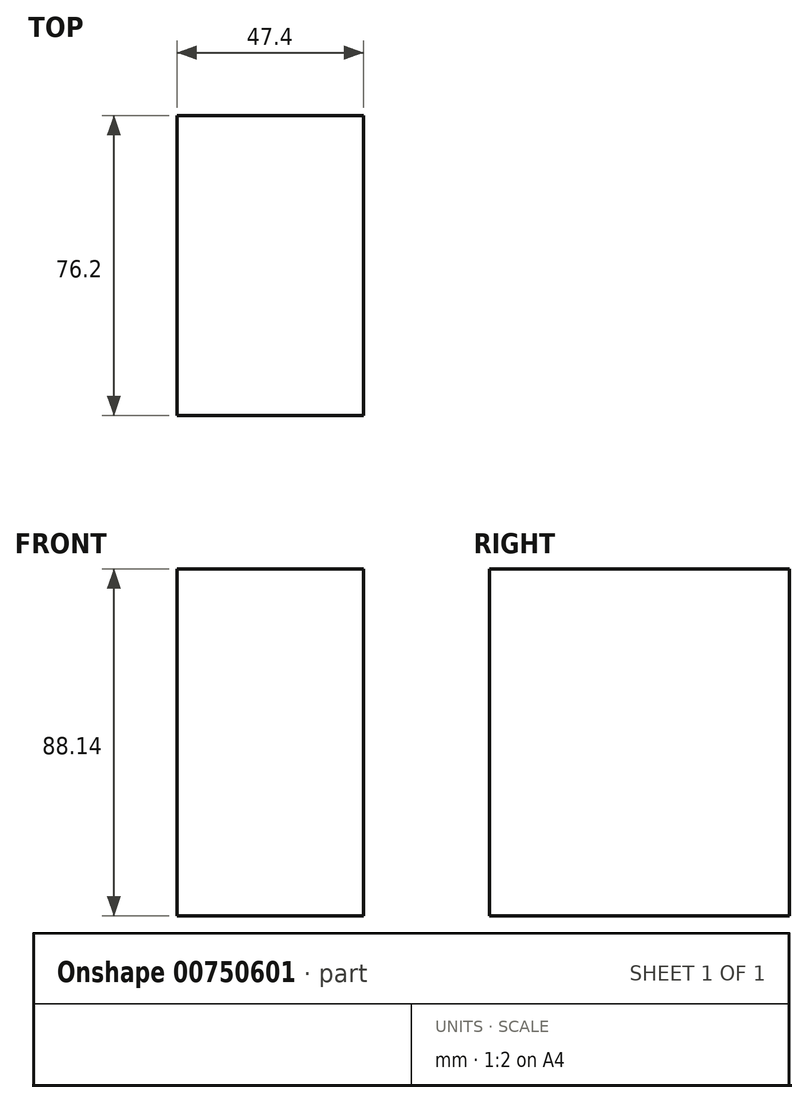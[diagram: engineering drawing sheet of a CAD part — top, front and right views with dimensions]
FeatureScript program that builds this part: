
annotation { "Feature Type Name" : "Feature", "Feature Type Description" : "" }
export const myFeature = defineFeature(function(context is Context, id is Id, definition is map)
    precondition{}
    {
        {
            var Q0;
            Q0=qCreatedBy(makeId("Front.planeOp"),FACE);
            var sketch = newSketch(context, id + "F0", { "sketchPlane" : qUnion([Q0])});
            skLineSegment(sketch, "E0.bottom", {"start": v(24.31, 28) * mm, "end": v(-23.09, 28) * mm});
            skLineSegment(sketch, "E0.top", {"start": v(24.31, -60.13) * mm, "end": v(-23.09, -60.13) * mm});
            skLineSegment(sketch, "E0.left", {"start": v(24.31, 28) * mm, "end": v(24.31, -60.13) * mm});
            skLineSegment(sketch, "E0.right", {"start": v(-23.09, 28) * mm, "end": v(-23.09, -60.13) * mm});
            skSolve(sketch);
        }
        {
            var Q0;
            Q0=makeQuery(id+"F0.imprint","IMPRINT",FACE,{"disambiguationData":[TD([[makeQuery(id+"F0.imprint","IMPRINT",EDGE,{"derivedFrom":sQuery(id+"F0.wireOp",EDGE,"E0.bottom")}),1.0]])]});
            extrude(context, id + "F1", {"entities" : qUnion([Q0]), "depth" : 76.2 * mm, "offsetDistance" : 25.4 * mm});
        }
    });
